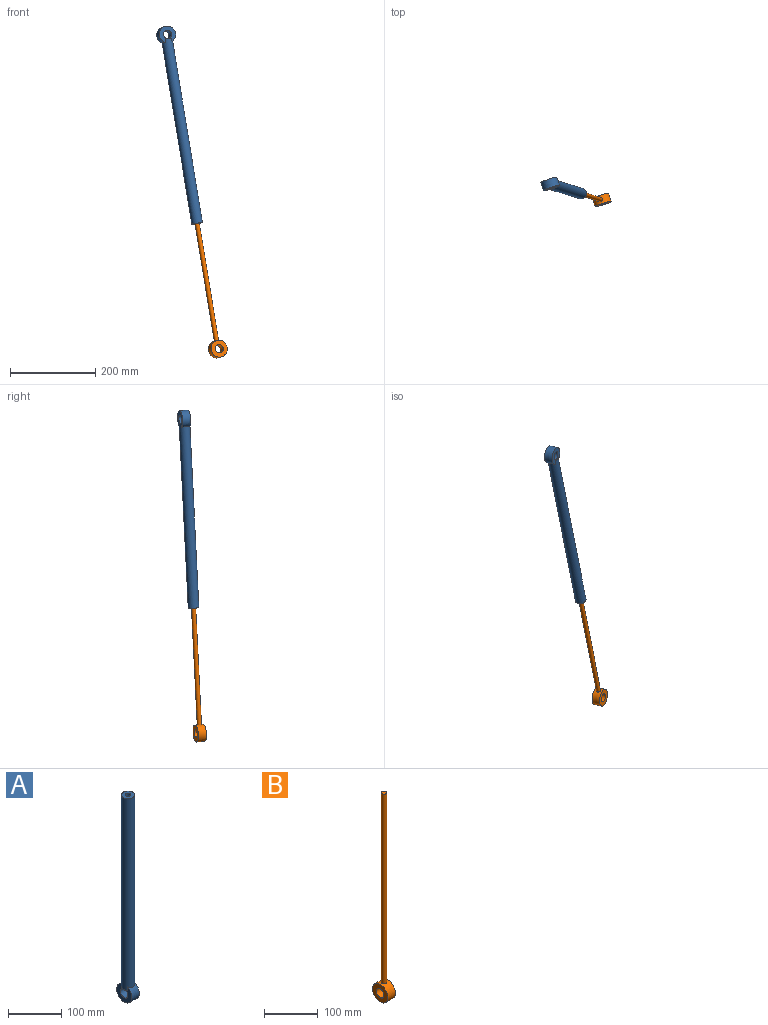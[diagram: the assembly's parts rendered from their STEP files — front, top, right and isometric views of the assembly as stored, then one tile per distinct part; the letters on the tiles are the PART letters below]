
ASSEMBLY  parts=2 mates=1
PART A: 10 faces, bbox 25x40x470 mm
  f0: cylinder r=20mm len=40mm, axis (-1,0,0), area 2045.8mm2, adj f1,f2,f6
  f1: plane 40x38.54mm, normal (1,0,0), area 799.7mm2, adj f0,f3,f6,f8
  f2: plane 40x38.54mm, normal (-1,0,0), area 799.7mm2, adj f0,f3,f5,f6
  f3: cylinder r=10mm len=20mm, axis (-1,0,0), area 1256.6mm2, adj f1,f2
  f4: cylinder r=5mm len=430.64mm, axis (0,0,-1), area 13518.8mm2, adj f7,f9
  f5: plane 15x2.5mm, normal (0,0,-1), area 25.5mm2, adj f2,f6
  f6: cylinder r=12.5mm len=440mm, axis (0,0,-1), area 34244.5mm2, adj f0,f1,f2,f5,f7,f8
  f7: plane 25x25mm, normal (0,0,1), area 412.3mm2, adj f4,f6
  f8: plane 15x2.5mm, normal (0,0,-1), area 25.5mm2, adj f1,f6
  f9: cylinder r=20mm len=10mm, axis (-1,0,0), area 79.2mm2, adj f4
PART B: 6 faces, bbox 20x40x470 mm
  f0: cylinder r=20mm len=40mm, axis (-1,0,0), area 2434mm2, adj f2,f3,f4
  f1: cylinder r=10mm len=20mm, axis (-1,0,0), area 1256.6mm2, adj f2,f3
  f2: plane 40x40mm, normal (1,0,0), area 942.5mm2, adj f0,f1
  f3: plane 40x40mm, normal (-1,0,0), area 942.5mm2, adj f0,f1
  f4: cylinder r=5mm len=430.64mm, axis (0,0,-1), area 13518.8mm2, adj f0,f5
  f5: plane 10x10mm, normal (0,0,1), area 78.5mm2, adj f4
PLACE A rot(axis=(-0.81,0.58,-0.08),176.8deg) t=(79.25,73.66,768.44)mm
PLACE B rot(axis=(0.05,-0.14,-0.99),72.3deg) t=(209.96,8.75,32.17)mm
MATE cylindrical A.f4 <-> B.f4  axis (-0.16,0.05,0.99) through (161.35,23.34,327.84)mm
